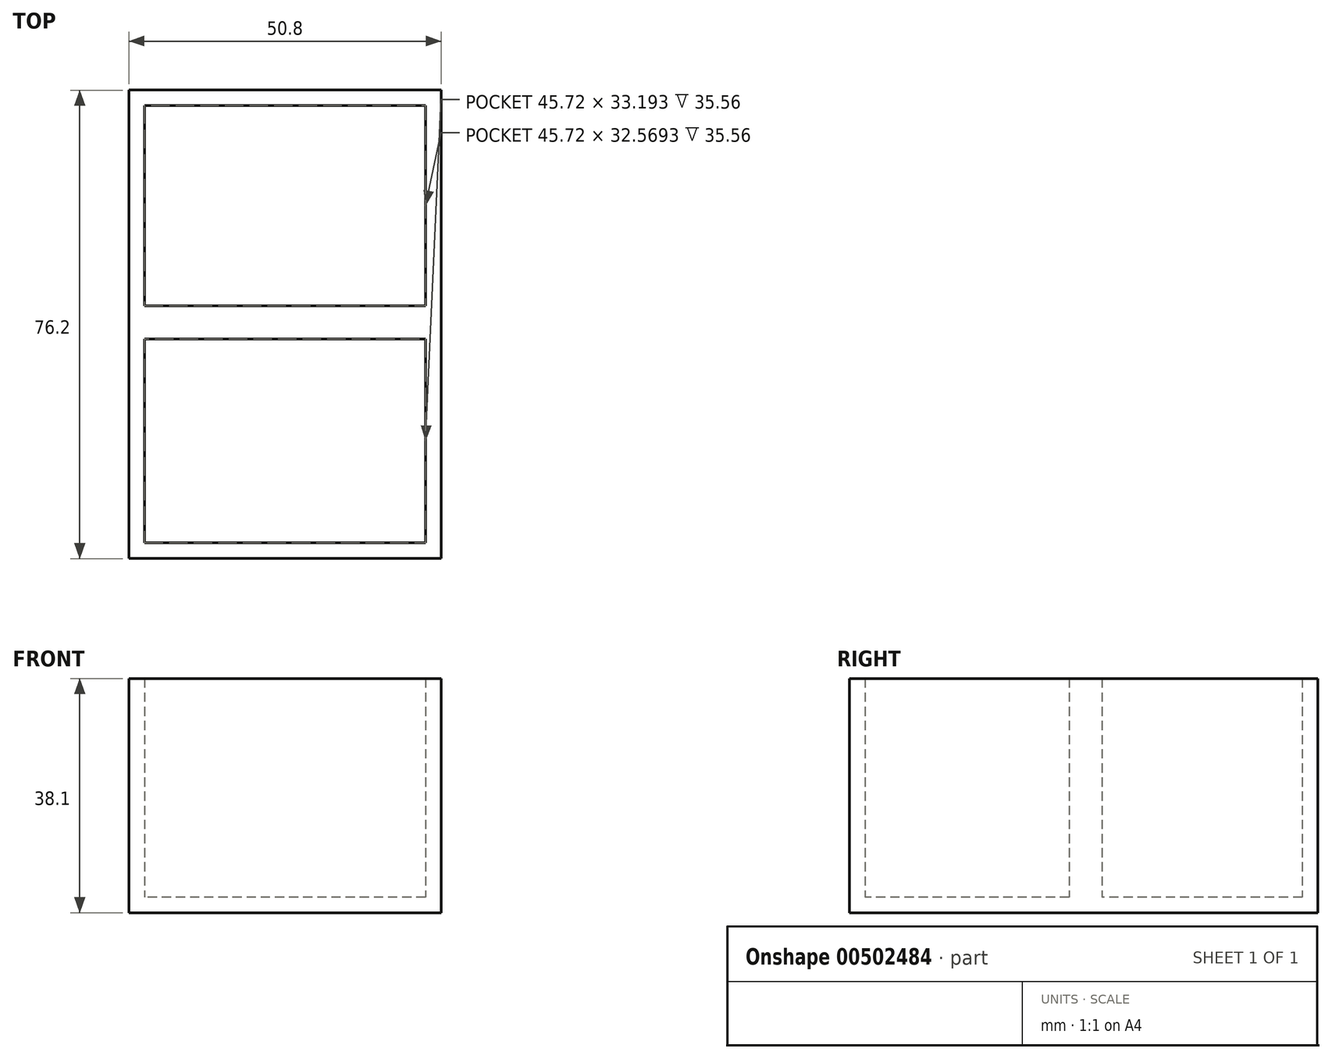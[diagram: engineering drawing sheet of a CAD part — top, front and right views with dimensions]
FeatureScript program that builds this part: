
annotation { "Feature Type Name" : "Feature", "Feature Type Description" : "" }
export const myFeature = defineFeature(function(context is Context, id is Id, definition is map)
    precondition{}
    {
        {
            var Q0;
            Q0=qCreatedBy(makeId("Top.planeOp"),FACE);
            var sketch = newSketch(context, id + "F0", { "sketchPlane" : qUnion([Q0])});
            skLineSegment(sketch, "E0.bottom", {"start": v(-21.23, 32.95) * mm, "end": v(29.57, 32.95) * mm});
            skLineSegment(sketch, "E0.top", {"start": v(-21.23, -43.25) * mm, "end": v(29.57, -43.25) * mm});
            skLineSegment(sketch, "E0.left", {"start": v(-21.23, 32.95) * mm, "end": v(-21.23, -43.25) * mm});
            skLineSegment(sketch, "E0.right", {"start": v(29.57, 32.95) * mm, "end": v(29.57, -43.25) * mm});
            skSolve(sketch);
        }
        {
            var Q0;
            Q0=makeQuery(id+"F0.imprint","IMPRINT",FACE,{"disambiguationData":[TD([[makeQuery(id+"F0.imprint","IMPRINT",EDGE,{"derivedFrom":sQuery(id+"F0.wireOp",EDGE,"E0.bottom")}),-1.0]])]});
            extrude(context, id + "F1", {"entities" : qUnion([Q0]), "depth" : 38.1 * mm});
        }
        {
            var Q0;
            Q0=makeQuery(id+"F1.opExtrude","CAP_FACE",FACE,{"disambiguationData":[OSD([sQuery(id+"F0.wireOp",EDGE,"E0.bottom"),sQuery(id+"F0.wireOp",EDGE,"E0.top"),sQuery(id+"F0.wireOp",EDGE,"E0.left"),sQuery(id+"F0.wireOp",EDGE,"E0.right")])],"isStart":false});
            shell(context, id + "F2", {"entities" : qUnion([Q0]), "thickness" : 2.54 * mm});
        }
        {
            var Q0;
            Q0=makeQuery(id+"F2.opShell","OFFSET_FACE",FACE,{"disambiguationData":[OSD([sQuery(id+"F0.wireOp",EDGE,"E0.bottom"),sQuery(id+"F0.wireOp",EDGE,"E0.top"),sQuery(id+"F0.wireOp",EDGE,"E0.left"),sQuery(id+"F0.wireOp",EDGE,"E0.right")])]});
            var sketch = newSketch(context, id + "F3", { "sketchPlane" : qUnion([Q0])});
            skLineSegment(sketch, "E1.bottom", {"start": v(-18.7, -5.15) * mm, "end": v(27.03, -5.15) * mm});
            skLineSegment(sketch, "E1.top", {"start": v(-18.7, -5.15) * mm, "end": v(27.03, -5.15) * mm});
            skLineSegment(sketch, "E1.left", {"start": v(-18.7, -5.15) * mm, "end": v(-18.7, -5.15) * mm});
            skLineSegment(sketch, "E1.right", {"start": v(27.03, -5.15) * mm, "end": v(27.03, -5.15) * mm});
            skLineSegment(sketch, "E2.bottom", {"start": v(27.03, -7.51) * mm, "end": v(-18.7, -7.51) * mm});
            skLineSegment(sketch, "E2.top", {"start": v(27.03, -2.16) * mm, "end": v(-18.7, -2.16) * mm});
            skLineSegment(sketch, "E2.left", {"start": v(27.03, -7.51) * mm, "end": v(27.03, -2.16) * mm});
            skLineSegment(sketch, "E2.right", {"start": v(-18.7, -7.51) * mm, "end": v(-18.7, -2.16) * mm});
            skSolve(sketch);
        }
        {
            var Q0;
            Q0 = qSketchRegion(id + "F3", true);
            extrude(context, id + "F4", {"entities" : qUnion([Q0]), "operationType" : NewBodyOperationType.ADD, "depth" : 35.56 * mm});
        }
    });
